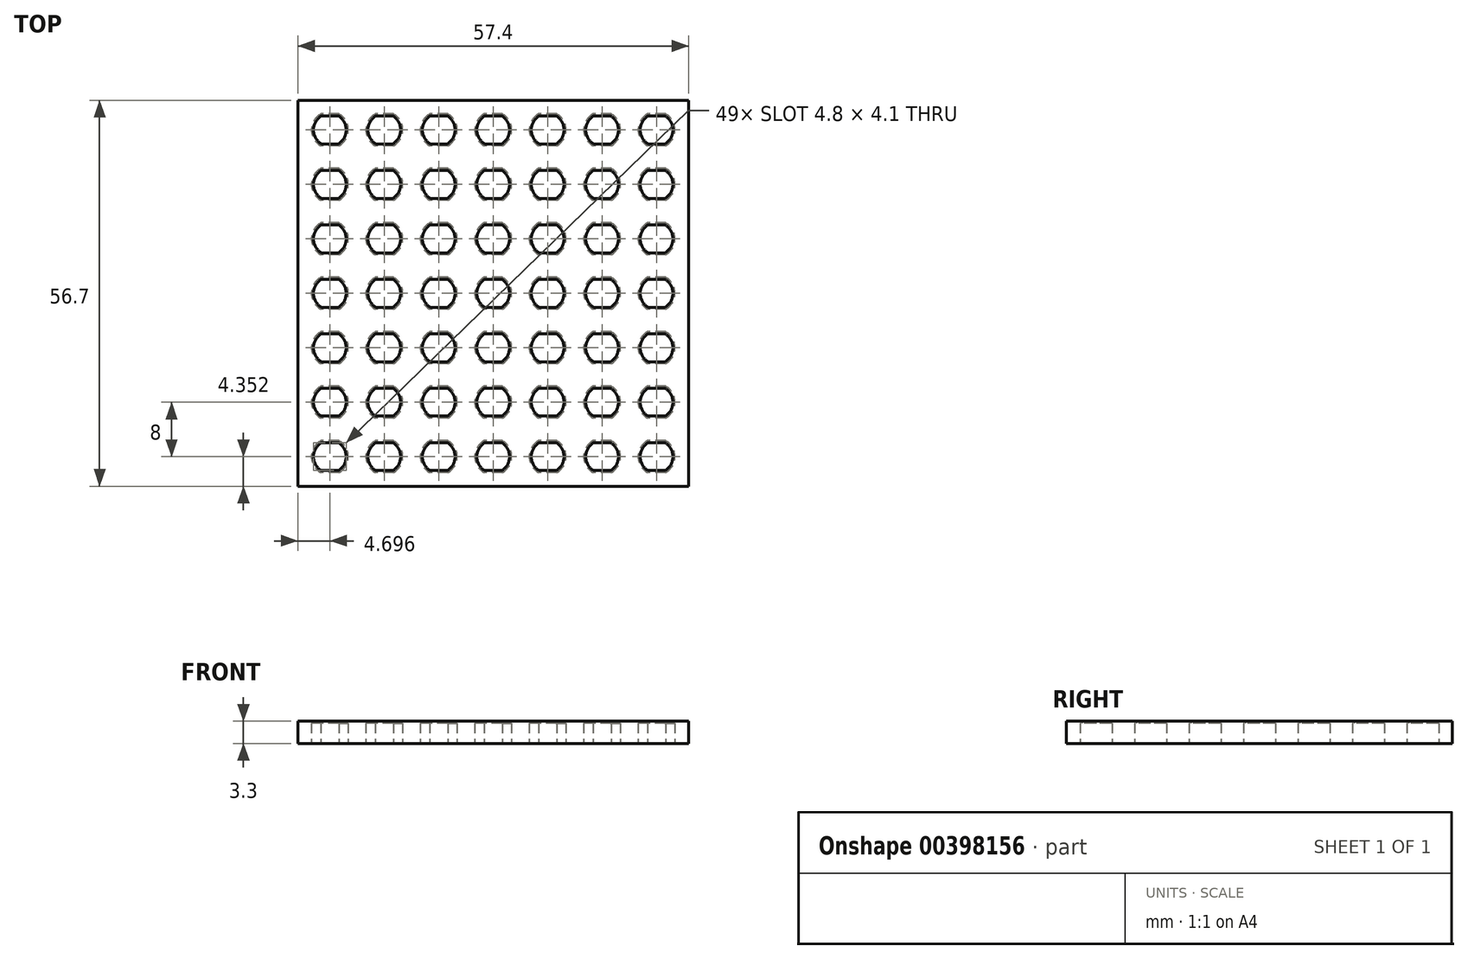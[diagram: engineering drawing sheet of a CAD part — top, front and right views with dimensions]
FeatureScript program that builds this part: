
annotation { "Feature Type Name" : "Feature", "Feature Type Description" : "" }
export const myFeature = defineFeature(function(context is Context, id is Id, definition is map)
    precondition{}
    {
        {
            var Q0;
            Q0=qCreatedBy(makeId("Top.planeOp"),FACE);
            var sketch = newSketch(context, id + "F0", { "sketchPlane" : qUnion([Q0])});
            skLineSegment(sketch, "E0.bottom", {"start": v(27.32, -19.22) * mm, "end": v(-27.32, -19.22) * mm, "construction": true});
            skLineSegment(sketch, "E0.top", {"start": v(27.32, 19.22) * mm, "end": v(-27.32, 19.22) * mm, "construction": true});
            skLineSegment(sketch, "E0.left", {"start": v(27.32, -19.22) * mm, "end": v(27.32, 19.22) * mm, "construction": true});
            skLineSegment(sketch, "E0.right", {"start": v(-27.32, -19.22) * mm, "end": v(-27.32, 19.22) * mm, "construction": true});
            skPoint(sketch, "E0.middle", {"position": v(0, 0) * mm});
            skArc(sketch, "E1", {"start": v(-23.3, 14.17) * mm, "mid": v(-21.92, 16.52) * mm, "end": v(-23.3, 18.87) * mm});
            skLineSegment(sketch, "E2.bottom", {"start": v(-23.3, 18.87) * mm, "end": v(-25.95, 18.87) * mm});
            skLineSegment(sketch, "E2.top", {"start": v(-23.3, 14.17) * mm, "end": v(-25.95, 14.17) * mm});
            skPoint(sketch, "E3.orphan", {"position": v(-21.92, 14.17) * mm});
            skPoint(sketch, "E4.orphan", {"position": v(-21.92, 18.87) * mm});
            skArc(sketch, "E5.trimOffspring", {"start": v(-25.95, 18.87) * mm, "mid": v(-27.32, 16.52) * mm, "end": v(-25.95, 14.17) * mm});
            skArc(sketch, "E6.0.1.0", {"start": v(-25.95, 10.87) * mm, "mid": v(-27.32, 8.52) * mm, "end": v(-25.95, 6.17) * mm});
            skLineSegment(sketch, "E6.0.1.1", {"start": v(-23.3, 6.17) * mm, "end": v(-25.95, 6.17) * mm});
            skLineSegment(sketch, "E6.0.1.2", {"start": v(-23.3, 10.87) * mm, "end": v(-25.95, 10.87) * mm});
            skArc(sketch, "E6.0.1.3", {"start": v(-23.3, 6.17) * mm, "mid": v(-21.92, 8.52) * mm, "end": v(-23.3, 10.87) * mm});
            skArc(sketch, "E6.0.2.0", {"start": v(-25.95, 2.87) * mm, "mid": v(-27.32, 0.52) * mm, "end": v(-25.95, -1.83) * mm});
            skLineSegment(sketch, "E6.0.2.1", {"start": v(-23.3, -1.83) * mm, "end": v(-25.95, -1.83) * mm});
            skLineSegment(sketch, "E6.0.2.2", {"start": v(-23.3, 2.87) * mm, "end": v(-25.95, 2.87) * mm});
            skArc(sketch, "E6.0.2.3", {"start": v(-23.3, -1.83) * mm, "mid": v(-21.92, 0.52) * mm, "end": v(-23.3, 2.87) * mm});
            skArc(sketch, "E6.1.0.0", {"start": v(-17.95, 18.87) * mm, "mid": v(-19.32, 16.52) * mm, "end": v(-17.95, 14.17) * mm});
            skLineSegment(sketch, "E6.1.0.1", {"start": v(-15.3, 14.17) * mm, "end": v(-17.95, 14.17) * mm});
            skLineSegment(sketch, "E6.1.0.2", {"start": v(-15.3, 18.87) * mm, "end": v(-17.95, 18.87) * mm});
            skArc(sketch, "E6.1.0.3", {"start": v(-15.3, 14.17) * mm, "mid": v(-13.92, 16.52) * mm, "end": v(-15.3, 18.87) * mm});
            skArc(sketch, "E6.1.1.0", {"start": v(-17.95, 10.87) * mm, "mid": v(-19.32, 8.52) * mm, "end": v(-17.95, 6.17) * mm});
            skLineSegment(sketch, "E6.1.1.1", {"start": v(-15.3, 6.17) * mm, "end": v(-17.95, 6.17) * mm});
            skLineSegment(sketch, "E6.1.1.2", {"start": v(-15.3, 10.87) * mm, "end": v(-17.95, 10.87) * mm});
            skArc(sketch, "E6.1.1.3", {"start": v(-15.3, 6.17) * mm, "mid": v(-13.92, 8.52) * mm, "end": v(-15.3, 10.87) * mm});
            skArc(sketch, "E6.1.2.0", {"start": v(-17.95, 2.87) * mm, "mid": v(-19.32, 0.52) * mm, "end": v(-17.95, -1.83) * mm});
            skLineSegment(sketch, "E6.1.2.1", {"start": v(-15.3, -1.83) * mm, "end": v(-17.95, -1.83) * mm});
            skLineSegment(sketch, "E6.1.2.2", {"start": v(-15.3, 2.87) * mm, "end": v(-17.95, 2.87) * mm});
            skArc(sketch, "E6.1.2.3", {"start": v(-15.3, -1.83) * mm, "mid": v(-13.92, 0.52) * mm, "end": v(-15.3, 2.87) * mm});
            skArc(sketch, "E6.2.0.0", {"start": v(-9.95, 18.87) * mm, "mid": v(-11.32, 16.52) * mm, "end": v(-9.95, 14.17) * mm});
            skLineSegment(sketch, "E6.2.0.1", {"start": v(-7.3, 14.17) * mm, "end": v(-9.95, 14.17) * mm});
            skLineSegment(sketch, "E6.2.0.2", {"start": v(-7.3, 18.87) * mm, "end": v(-9.95, 18.87) * mm});
            skArc(sketch, "E6.2.0.3", {"start": v(-7.3, 14.17) * mm, "mid": v(-5.92, 16.52) * mm, "end": v(-7.3, 18.87) * mm});
            skArc(sketch, "E6.2.1.0", {"start": v(-9.95, 10.87) * mm, "mid": v(-11.32, 8.52) * mm, "end": v(-9.95, 6.17) * mm});
            skLineSegment(sketch, "E6.2.1.1", {"start": v(-7.3, 6.17) * mm, "end": v(-9.95, 6.17) * mm});
            skLineSegment(sketch, "E6.2.1.2", {"start": v(-7.3, 10.87) * mm, "end": v(-9.95, 10.87) * mm});
            skArc(sketch, "E6.2.1.3", {"start": v(-7.3, 6.17) * mm, "mid": v(-5.92, 8.52) * mm, "end": v(-7.3, 10.87) * mm});
            skArc(sketch, "E6.2.2.0", {"start": v(-9.95, 2.87) * mm, "mid": v(-11.32, 0.52) * mm, "end": v(-9.95, -1.83) * mm});
            skLineSegment(sketch, "E6.2.2.1", {"start": v(-7.3, -1.83) * mm, "end": v(-9.95, -1.83) * mm});
            skLineSegment(sketch, "E6.2.2.2", {"start": v(-7.3, 2.87) * mm, "end": v(-9.95, 2.87) * mm});
            skArc(sketch, "E6.2.2.3", {"start": v(-7.3, -1.83) * mm, "mid": v(-5.92, 0.52) * mm, "end": v(-7.3, 2.87) * mm});
            skArc(sketch, "E6.3.0.0", {"start": v(-1.95, 18.87) * mm, "mid": v(-3.32, 16.52) * mm, "end": v(-1.95, 14.17) * mm});
            skLineSegment(sketch, "E6.3.0.1", {"start": v(0.7, 14.17) * mm, "end": v(-1.95, 14.17) * mm});
            skLineSegment(sketch, "E6.3.0.2", {"start": v(0.7, 18.87) * mm, "end": v(-1.95, 18.87) * mm});
            skArc(sketch, "E6.3.0.3", {"start": v(0.7, 14.17) * mm, "mid": v(2.08, 16.52) * mm, "end": v(0.7, 18.87) * mm});
            skArc(sketch, "E6.3.1.0", {"start": v(-1.95, 10.87) * mm, "mid": v(-3.32, 8.52) * mm, "end": v(-1.95, 6.17) * mm});
            skLineSegment(sketch, "E6.3.1.1", {"start": v(0.7, 6.17) * mm, "end": v(-1.95, 6.17) * mm});
            skLineSegment(sketch, "E6.3.1.2", {"start": v(0.7, 10.87) * mm, "end": v(-1.95, 10.87) * mm});
            skArc(sketch, "E6.3.1.3", {"start": v(0.7, 6.17) * mm, "mid": v(2.08, 8.52) * mm, "end": v(0.7, 10.87) * mm});
            skArc(sketch, "E6.3.2.0", {"start": v(-1.95, 2.87) * mm, "mid": v(-3.32, 0.52) * mm, "end": v(-1.95, -1.83) * mm});
            skLineSegment(sketch, "E6.3.2.1", {"start": v(0.7, -1.83) * mm, "end": v(-1.95, -1.83) * mm});
            skLineSegment(sketch, "E6.3.2.2", {"start": v(0.7, 2.87) * mm, "end": v(-1.95, 2.87) * mm});
            skArc(sketch, "E6.3.2.3", {"start": v(0.7, -1.83) * mm, "mid": v(2.08, 0.52) * mm, "end": v(0.7, 2.87) * mm});
            skLineSegment(sketch, "E6.direction1", {"start": v(-25.95, 14.17) * mm, "end": v(-17.95, 14.17) * mm, "construction": true});
            skLineSegment(sketch, "E6.direction2", {"start": v(-25.95, 14.17) * mm, "end": v(-25.95, 6.17) * mm, "construction": true});
            skLineSegment(sketch, "E7.bottom", {"start": v(-29.32, 20.87) * mm, "end": v(28.08, 20.87) * mm});
            skLineSegment(sketch, "E7.top", {"start": v(-29.32, -35.83) * mm, "end": v(28.08, -35.83) * mm});
            skLineSegment(sketch, "E7.left", {"start": v(-29.32, 20.87) * mm, "end": v(-29.32, -35.83) * mm});
            skLineSegment(sketch, "E7.right", {"start": v(28.08, 20.87) * mm, "end": v(28.08, -35.83) * mm});
            skArc(sketch, "E8.0.4.0", {"start": v(6.05, 18.87) * mm, "mid": v(4.68, 16.52) * mm, "end": v(6.05, 14.17) * mm});
            skLineSegment(sketch, "E8.4.4.0", {"start": v(8.7, 14.17) * mm, "end": v(6.05, 14.17) * mm});
            skLineSegment(sketch, "E8.7.4.0", {"start": v(8.7, 18.87) * mm, "end": v(6.05, 18.87) * mm});
            skArc(sketch, "E8.10.4.0", {"start": v(8.7, 14.17) * mm, "mid": v(10.08, 16.52) * mm, "end": v(8.7, 18.87) * mm});
            skArc(sketch, "E8.0.4.1", {"start": v(6.05, 10.87) * mm, "mid": v(4.68, 8.52) * mm, "end": v(6.05, 6.17) * mm});
            skLineSegment(sketch, "E8.4.4.1", {"start": v(8.7, 6.17) * mm, "end": v(6.05, 6.17) * mm});
            skLineSegment(sketch, "E8.7.4.1", {"start": v(8.7, 10.87) * mm, "end": v(6.05, 10.87) * mm});
            skArc(sketch, "E8.10.4.1", {"start": v(8.7, 6.17) * mm, "mid": v(10.08, 8.52) * mm, "end": v(8.7, 10.87) * mm});
            skArc(sketch, "E8.0.4.2", {"start": v(6.05, 2.87) * mm, "mid": v(4.68, 0.52) * mm, "end": v(6.05, -1.83) * mm});
            skLineSegment(sketch, "E8.4.4.2", {"start": v(8.7, -1.83) * mm, "end": v(6.05, -1.83) * mm});
            skLineSegment(sketch, "E8.7.4.2", {"start": v(8.7, 2.87) * mm, "end": v(6.05, 2.87) * mm});
            skArc(sketch, "E8.10.4.2", {"start": v(8.7, -1.83) * mm, "mid": v(10.08, 0.52) * mm, "end": v(8.7, 2.87) * mm});
            skArc(sketch, "E8.0.5.0", {"start": v(14.05, 18.87) * mm, "mid": v(12.68, 16.52) * mm, "end": v(14.05, 14.17) * mm});
            skLineSegment(sketch, "E8.4.5.0", {"start": v(16.7, 14.17) * mm, "end": v(14.05, 14.17) * mm});
            skLineSegment(sketch, "E8.7.5.0", {"start": v(16.7, 18.87) * mm, "end": v(14.05, 18.87) * mm});
            skArc(sketch, "E8.10.5.0", {"start": v(16.7, 14.17) * mm, "mid": v(18.08, 16.52) * mm, "end": v(16.7, 18.87) * mm});
            skArc(sketch, "E8.0.5.1", {"start": v(14.05, 10.87) * mm, "mid": v(12.68, 8.52) * mm, "end": v(14.05, 6.17) * mm});
            skLineSegment(sketch, "E8.4.5.1", {"start": v(16.7, 6.17) * mm, "end": v(14.05, 6.17) * mm});
            skLineSegment(sketch, "E8.7.5.1", {"start": v(16.7, 10.87) * mm, "end": v(14.05, 10.87) * mm});
            skArc(sketch, "E8.10.5.1", {"start": v(16.7, 6.17) * mm, "mid": v(18.08, 8.52) * mm, "end": v(16.7, 10.87) * mm});
            skArc(sketch, "E8.0.5.2", {"start": v(14.05, 2.87) * mm, "mid": v(12.68, 0.52) * mm, "end": v(14.05, -1.83) * mm});
            skLineSegment(sketch, "E8.4.5.2", {"start": v(16.7, -1.83) * mm, "end": v(14.05, -1.83) * mm});
            skLineSegment(sketch, "E8.7.5.2", {"start": v(16.7, 2.87) * mm, "end": v(14.05, 2.87) * mm});
            skArc(sketch, "E8.10.5.2", {"start": v(16.7, -1.83) * mm, "mid": v(18.08, 0.52) * mm, "end": v(16.7, 2.87) * mm});
            skArc(sketch, "E8.0.6.0", {"start": v(22.05, 18.87) * mm, "mid": v(20.68, 16.52) * mm, "end": v(22.05, 14.17) * mm});
            skLineSegment(sketch, "E8.4.6.0", {"start": v(24.7, 14.17) * mm, "end": v(22.05, 14.17) * mm});
            skLineSegment(sketch, "E8.7.6.0", {"start": v(24.7, 18.87) * mm, "end": v(22.05, 18.87) * mm});
            skArc(sketch, "E8.10.6.0", {"start": v(24.7, 14.17) * mm, "mid": v(26.08, 16.52) * mm, "end": v(24.7, 18.87) * mm});
            skArc(sketch, "E8.0.6.1", {"start": v(22.05, 10.87) * mm, "mid": v(20.68, 8.52) * mm, "end": v(22.05, 6.17) * mm});
            skLineSegment(sketch, "E8.4.6.1", {"start": v(24.7, 6.17) * mm, "end": v(22.05, 6.17) * mm});
            skLineSegment(sketch, "E8.7.6.1", {"start": v(24.7, 10.87) * mm, "end": v(22.05, 10.87) * mm});
            skArc(sketch, "E8.10.6.1", {"start": v(24.7, 6.17) * mm, "mid": v(26.08, 8.52) * mm, "end": v(24.7, 10.87) * mm});
            skArc(sketch, "E8.0.6.2", {"start": v(22.05, 2.87) * mm, "mid": v(20.68, 0.52) * mm, "end": v(22.05, -1.83) * mm});
            skLineSegment(sketch, "E8.4.6.2", {"start": v(24.7, -1.83) * mm, "end": v(22.05, -1.83) * mm});
            skLineSegment(sketch, "E8.7.6.2", {"start": v(24.7, 2.87) * mm, "end": v(22.05, 2.87) * mm});
            skArc(sketch, "E8.10.6.2", {"start": v(24.7, -1.83) * mm, "mid": v(26.08, 0.52) * mm, "end": v(24.7, 2.87) * mm});
            skArc(sketch, "E9.0.0.3", {"start": v(-25.95, -5.13) * mm, "mid": v(-27.32, -7.48) * mm, "end": v(-25.95, -9.83) * mm});
            skLineSegment(sketch, "E9.4.0.3", {"start": v(-23.3, -9.83) * mm, "end": v(-25.95, -9.83) * mm});
            skLineSegment(sketch, "E9.7.0.3", {"start": v(-23.3, -5.13) * mm, "end": v(-25.95, -5.13) * mm});
            skArc(sketch, "E9.10.0.3", {"start": v(-23.3, -9.83) * mm, "mid": v(-21.92, -7.48) * mm, "end": v(-23.3, -5.13) * mm});
            skArc(sketch, "E9.0.0.4", {"start": v(-25.95, -13.13) * mm, "mid": v(-27.32, -15.48) * mm, "end": v(-25.95, -17.83) * mm});
            skLineSegment(sketch, "E9.4.0.4", {"start": v(-23.3, -17.83) * mm, "end": v(-25.95, -17.83) * mm});
            skLineSegment(sketch, "E9.7.0.4", {"start": v(-23.3, -13.13) * mm, "end": v(-25.95, -13.13) * mm});
            skArc(sketch, "E9.10.0.4", {"start": v(-23.3, -17.83) * mm, "mid": v(-21.92, -15.48) * mm, "end": v(-23.3, -13.13) * mm});
            skArc(sketch, "E9.0.0.5", {"start": v(-25.95, -21.13) * mm, "mid": v(-27.32, -23.48) * mm, "end": v(-25.95, -25.83) * mm});
            skLineSegment(sketch, "E9.4.0.5", {"start": v(-23.3, -25.83) * mm, "end": v(-25.95, -25.83) * mm});
            skLineSegment(sketch, "E9.7.0.5", {"start": v(-23.3, -21.13) * mm, "end": v(-25.95, -21.13) * mm});
            skArc(sketch, "E9.10.0.5", {"start": v(-23.3, -25.83) * mm, "mid": v(-21.92, -23.48) * mm, "end": v(-23.3, -21.13) * mm});
            skArc(sketch, "E9.0.0.6", {"start": v(-25.95, -29.13) * mm, "mid": v(-27.32, -31.48) * mm, "end": v(-25.95, -33.83) * mm});
            skLineSegment(sketch, "E9.4.0.6", {"start": v(-23.3, -33.83) * mm, "end": v(-25.95, -33.83) * mm});
            skLineSegment(sketch, "E9.7.0.6", {"start": v(-23.3, -29.13) * mm, "end": v(-25.95, -29.13) * mm});
            skArc(sketch, "E9.10.0.6", {"start": v(-23.3, -33.83) * mm, "mid": v(-21.92, -31.48) * mm, "end": v(-23.3, -29.13) * mm});
            skArc(sketch, "E9.0.1.3", {"start": v(-17.95, -5.13) * mm, "mid": v(-19.32, -7.48) * mm, "end": v(-17.95, -9.83) * mm});
            skLineSegment(sketch, "E9.4.1.3", {"start": v(-15.3, -9.83) * mm, "end": v(-17.95, -9.83) * mm});
            skLineSegment(sketch, "E9.7.1.3", {"start": v(-15.3, -5.13) * mm, "end": v(-17.95, -5.13) * mm});
            skArc(sketch, "E9.10.1.3", {"start": v(-15.3, -9.83) * mm, "mid": v(-13.92, -7.48) * mm, "end": v(-15.3, -5.13) * mm});
            skArc(sketch, "E9.0.1.4", {"start": v(-17.95, -13.13) * mm, "mid": v(-19.32, -15.48) * mm, "end": v(-17.95, -17.83) * mm});
            skLineSegment(sketch, "E9.4.1.4", {"start": v(-15.3, -17.83) * mm, "end": v(-17.95, -17.83) * mm});
            skLineSegment(sketch, "E9.7.1.4", {"start": v(-15.3, -13.13) * mm, "end": v(-17.95, -13.13) * mm});
            skArc(sketch, "E9.10.1.4", {"start": v(-15.3, -17.83) * mm, "mid": v(-13.92, -15.48) * mm, "end": v(-15.3, -13.13) * mm});
            skArc(sketch, "E9.0.1.5", {"start": v(-17.95, -21.13) * mm, "mid": v(-19.32, -23.48) * mm, "end": v(-17.95, -25.83) * mm});
            skLineSegment(sketch, "E9.4.1.5", {"start": v(-15.3, -25.83) * mm, "end": v(-17.95, -25.83) * mm});
            skLineSegment(sketch, "E9.7.1.5", {"start": v(-15.3, -21.13) * mm, "end": v(-17.95, -21.13) * mm});
            skArc(sketch, "E9.10.1.5", {"start": v(-15.3, -25.83) * mm, "mid": v(-13.92, -23.48) * mm, "end": v(-15.3, -21.13) * mm});
            skArc(sketch, "E9.0.1.6", {"start": v(-17.95, -29.13) * mm, "mid": v(-19.32, -31.48) * mm, "end": v(-17.95, -33.83) * mm});
            skLineSegment(sketch, "E9.4.1.6", {"start": v(-15.3, -33.83) * mm, "end": v(-17.95, -33.83) * mm});
            skLineSegment(sketch, "E9.7.1.6", {"start": v(-15.3, -29.13) * mm, "end": v(-17.95, -29.13) * mm});
            skArc(sketch, "E9.10.1.6", {"start": v(-15.3, -33.83) * mm, "mid": v(-13.92, -31.48) * mm, "end": v(-15.3, -29.13) * mm});
            skArc(sketch, "E9.0.2.3", {"start": v(-9.95, -5.13) * mm, "mid": v(-11.32, -7.48) * mm, "end": v(-9.95, -9.83) * mm});
            skLineSegment(sketch, "E9.4.2.3", {"start": v(-7.3, -9.83) * mm, "end": v(-9.95, -9.83) * mm});
            skLineSegment(sketch, "E9.7.2.3", {"start": v(-7.3, -5.13) * mm, "end": v(-9.95, -5.13) * mm});
            skArc(sketch, "E9.10.2.3", {"start": v(-7.3, -9.83) * mm, "mid": v(-5.92, -7.48) * mm, "end": v(-7.3, -5.13) * mm});
            skArc(sketch, "E9.0.2.4", {"start": v(-9.95, -13.13) * mm, "mid": v(-11.32, -15.48) * mm, "end": v(-9.95, -17.83) * mm});
            skLineSegment(sketch, "E9.4.2.4", {"start": v(-7.3, -17.83) * mm, "end": v(-9.95, -17.83) * mm});
            skLineSegment(sketch, "E9.7.2.4", {"start": v(-7.3, -13.13) * mm, "end": v(-9.95, -13.13) * mm});
            skArc(sketch, "E9.10.2.4", {"start": v(-7.3, -17.83) * mm, "mid": v(-5.92, -15.48) * mm, "end": v(-7.3, -13.13) * mm});
            skArc(sketch, "E9.0.2.5", {"start": v(-9.95, -21.13) * mm, "mid": v(-11.32, -23.48) * mm, "end": v(-9.95, -25.83) * mm});
            skLineSegment(sketch, "E9.4.2.5", {"start": v(-7.3, -25.83) * mm, "end": v(-9.95, -25.83) * mm});
            skLineSegment(sketch, "E9.7.2.5", {"start": v(-7.3, -21.13) * mm, "end": v(-9.95, -21.13) * mm});
            skArc(sketch, "E9.10.2.5", {"start": v(-7.3, -25.83) * mm, "mid": v(-5.92, -23.48) * mm, "end": v(-7.3, -21.13) * mm});
            skArc(sketch, "E9.0.2.6", {"start": v(-9.95, -29.13) * mm, "mid": v(-11.32, -31.48) * mm, "end": v(-9.95, -33.83) * mm});
            skLineSegment(sketch, "E9.4.2.6", {"start": v(-7.3, -33.83) * mm, "end": v(-9.95, -33.83) * mm});
            skLineSegment(sketch, "E9.7.2.6", {"start": v(-7.3, -29.13) * mm, "end": v(-9.95, -29.13) * mm});
            skArc(sketch, "E9.10.2.6", {"start": v(-7.3, -33.83) * mm, "mid": v(-5.92, -31.48) * mm, "end": v(-7.3, -29.13) * mm});
            skArc(sketch, "E9.0.3.3", {"start": v(-1.95, -5.13) * mm, "mid": v(-3.32, -7.48) * mm, "end": v(-1.95, -9.83) * mm});
            skLineSegment(sketch, "E9.4.3.3", {"start": v(0.7, -9.83) * mm, "end": v(-1.95, -9.83) * mm});
            skLineSegment(sketch, "E9.7.3.3", {"start": v(0.7, -5.13) * mm, "end": v(-1.95, -5.13) * mm});
            skArc(sketch, "E9.10.3.3", {"start": v(0.7, -9.83) * mm, "mid": v(2.08, -7.48) * mm, "end": v(0.7, -5.13) * mm});
            skArc(sketch, "E9.0.3.4", {"start": v(-1.95, -13.13) * mm, "mid": v(-3.32, -15.48) * mm, "end": v(-1.95, -17.83) * mm});
            skLineSegment(sketch, "E9.4.3.4", {"start": v(0.7, -17.83) * mm, "end": v(-1.95, -17.83) * mm});
            skLineSegment(sketch, "E9.7.3.4", {"start": v(0.7, -13.13) * mm, "end": v(-1.95, -13.13) * mm});
            skArc(sketch, "E9.10.3.4", {"start": v(0.7, -17.83) * mm, "mid": v(2.08, -15.48) * mm, "end": v(0.7, -13.13) * mm});
            skArc(sketch, "E9.0.3.5", {"start": v(-1.95, -21.13) * mm, "mid": v(-3.32, -23.48) * mm, "end": v(-1.95, -25.83) * mm});
            skLineSegment(sketch, "E9.4.3.5", {"start": v(0.7, -25.83) * mm, "end": v(-1.95, -25.83) * mm});
            skLineSegment(sketch, "E9.7.3.5", {"start": v(0.7, -21.13) * mm, "end": v(-1.95, -21.13) * mm});
            skArc(sketch, "E9.10.3.5", {"start": v(0.7, -25.83) * mm, "mid": v(2.08, -23.48) * mm, "end": v(0.7, -21.13) * mm});
            skArc(sketch, "E9.0.3.6", {"start": v(-1.95, -29.13) * mm, "mid": v(-3.32, -31.48) * mm, "end": v(-1.95, -33.83) * mm});
            skLineSegment(sketch, "E9.4.3.6", {"start": v(0.7, -33.83) * mm, "end": v(-1.95, -33.83) * mm});
            skLineSegment(sketch, "E9.7.3.6", {"start": v(0.7, -29.13) * mm, "end": v(-1.95, -29.13) * mm});
            skArc(sketch, "E9.10.3.6", {"start": v(0.7, -33.83) * mm, "mid": v(2.08, -31.48) * mm, "end": v(0.7, -29.13) * mm});
            skArc(sketch, "E9.0.4.3", {"start": v(6.05, -5.13) * mm, "mid": v(4.68, -7.48) * mm, "end": v(6.05, -9.83) * mm});
            skLineSegment(sketch, "E9.4.4.3", {"start": v(8.7, -9.83) * mm, "end": v(6.05, -9.83) * mm});
            skLineSegment(sketch, "E9.7.4.3", {"start": v(8.7, -5.13) * mm, "end": v(6.05, -5.13) * mm});
            skArc(sketch, "E9.10.4.3", {"start": v(8.7, -9.83) * mm, "mid": v(10.08, -7.48) * mm, "end": v(8.7, -5.13) * mm});
            skArc(sketch, "E9.0.4.4", {"start": v(6.05, -13.13) * mm, "mid": v(4.68, -15.48) * mm, "end": v(6.05, -17.83) * mm});
            skLineSegment(sketch, "E9.4.4.4", {"start": v(8.7, -17.83) * mm, "end": v(6.05, -17.83) * mm});
            skLineSegment(sketch, "E9.7.4.4", {"start": v(8.7, -13.13) * mm, "end": v(6.05, -13.13) * mm});
            skArc(sketch, "E9.10.4.4", {"start": v(8.7, -17.83) * mm, "mid": v(10.08, -15.48) * mm, "end": v(8.7, -13.13) * mm});
            skArc(sketch, "E9.0.4.5", {"start": v(6.05, -21.13) * mm, "mid": v(4.68, -23.48) * mm, "end": v(6.05, -25.83) * mm});
            skLineSegment(sketch, "E9.4.4.5", {"start": v(8.7, -25.83) * mm, "end": v(6.05, -25.83) * mm});
            skLineSegment(sketch, "E9.7.4.5", {"start": v(8.7, -21.13) * mm, "end": v(6.05, -21.13) * mm});
            skArc(sketch, "E9.10.4.5", {"start": v(8.7, -25.83) * mm, "mid": v(10.08, -23.48) * mm, "end": v(8.7, -21.13) * mm});
            skArc(sketch, "E9.0.4.6", {"start": v(6.05, -29.13) * mm, "mid": v(4.68, -31.48) * mm, "end": v(6.05, -33.83) * mm});
            skLineSegment(sketch, "E9.4.4.6", {"start": v(8.7, -33.83) * mm, "end": v(6.05, -33.83) * mm});
            skLineSegment(sketch, "E9.7.4.6", {"start": v(8.7, -29.13) * mm, "end": v(6.05, -29.13) * mm});
            skArc(sketch, "E9.10.4.6", {"start": v(8.7, -33.83) * mm, "mid": v(10.08, -31.48) * mm, "end": v(8.7, -29.13) * mm});
            skArc(sketch, "E9.0.5.3", {"start": v(14.05, -5.13) * mm, "mid": v(12.68, -7.48) * mm, "end": v(14.05, -9.83) * mm});
            skLineSegment(sketch, "E9.4.5.3", {"start": v(16.7, -9.83) * mm, "end": v(14.05, -9.83) * mm});
            skLineSegment(sketch, "E9.7.5.3", {"start": v(16.7, -5.13) * mm, "end": v(14.05, -5.13) * mm});
            skArc(sketch, "E9.10.5.3", {"start": v(16.7, -9.83) * mm, "mid": v(18.08, -7.48) * mm, "end": v(16.7, -5.13) * mm});
            skArc(sketch, "E9.0.5.4", {"start": v(14.05, -13.13) * mm, "mid": v(12.68, -15.48) * mm, "end": v(14.05, -17.83) * mm});
            skLineSegment(sketch, "E9.4.5.4", {"start": v(16.7, -17.83) * mm, "end": v(14.05, -17.83) * mm});
            skLineSegment(sketch, "E9.7.5.4", {"start": v(16.7, -13.13) * mm, "end": v(14.05, -13.13) * mm});
            skArc(sketch, "E9.10.5.4", {"start": v(16.7, -17.83) * mm, "mid": v(18.08, -15.48) * mm, "end": v(16.7, -13.13) * mm});
            skArc(sketch, "E9.0.5.5", {"start": v(14.05, -21.13) * mm, "mid": v(12.68, -23.48) * mm, "end": v(14.05, -25.83) * mm});
            skLineSegment(sketch, "E9.4.5.5", {"start": v(16.7, -25.83) * mm, "end": v(14.05, -25.83) * mm});
            skLineSegment(sketch, "E9.7.5.5", {"start": v(16.7, -21.13) * mm, "end": v(14.05, -21.13) * mm});
            skArc(sketch, "E9.10.5.5", {"start": v(16.7, -25.83) * mm, "mid": v(18.08, -23.48) * mm, "end": v(16.7, -21.13) * mm});
            skArc(sketch, "E9.0.5.6", {"start": v(14.05, -29.13) * mm, "mid": v(12.68, -31.48) * mm, "end": v(14.05, -33.83) * mm});
            skLineSegment(sketch, "E9.4.5.6", {"start": v(16.7, -33.83) * mm, "end": v(14.05, -33.83) * mm});
            skLineSegment(sketch, "E9.7.5.6", {"start": v(16.7, -29.13) * mm, "end": v(14.05, -29.13) * mm});
            skArc(sketch, "E9.10.5.6", {"start": v(16.7, -33.83) * mm, "mid": v(18.08, -31.48) * mm, "end": v(16.7, -29.13) * mm});
            skArc(sketch, "E9.0.6.3", {"start": v(22.05, -5.13) * mm, "mid": v(20.68, -7.48) * mm, "end": v(22.05, -9.83) * mm});
            skLineSegment(sketch, "E9.4.6.3", {"start": v(24.7, -9.83) * mm, "end": v(22.05, -9.83) * mm});
            skLineSegment(sketch, "E9.7.6.3", {"start": v(24.7, -5.13) * mm, "end": v(22.05, -5.13) * mm});
            skArc(sketch, "E9.10.6.3", {"start": v(24.7, -9.83) * mm, "mid": v(26.08, -7.48) * mm, "end": v(24.7, -5.13) * mm});
            skArc(sketch, "E9.0.6.4", {"start": v(22.05, -13.13) * mm, "mid": v(20.68, -15.48) * mm, "end": v(22.05, -17.83) * mm});
            skLineSegment(sketch, "E9.4.6.4", {"start": v(24.7, -17.83) * mm, "end": v(22.05, -17.83) * mm});
            skLineSegment(sketch, "E9.7.6.4", {"start": v(24.7, -13.13) * mm, "end": v(22.05, -13.13) * mm});
            skArc(sketch, "E9.10.6.4", {"start": v(24.7, -17.83) * mm, "mid": v(26.08, -15.48) * mm, "end": v(24.7, -13.13) * mm});
            skArc(sketch, "E9.0.6.5", {"start": v(22.05, -21.13) * mm, "mid": v(20.68, -23.48) * mm, "end": v(22.05, -25.83) * mm});
            skLineSegment(sketch, "E9.4.6.5", {"start": v(24.7, -25.83) * mm, "end": v(22.05, -25.83) * mm});
            skLineSegment(sketch, "E9.7.6.5", {"start": v(24.7, -21.13) * mm, "end": v(22.05, -21.13) * mm});
            skArc(sketch, "E9.10.6.5", {"start": v(24.7, -25.83) * mm, "mid": v(26.08, -23.48) * mm, "end": v(24.7, -21.13) * mm});
            skArc(sketch, "E9.0.6.6", {"start": v(22.05, -29.13) * mm, "mid": v(20.68, -31.48) * mm, "end": v(22.05, -33.83) * mm});
            skLineSegment(sketch, "E9.4.6.6", {"start": v(24.7, -33.83) * mm, "end": v(22.05, -33.83) * mm});
            skLineSegment(sketch, "E9.7.6.6", {"start": v(24.7, -29.13) * mm, "end": v(22.05, -29.13) * mm});
            skArc(sketch, "E9.10.6.6", {"start": v(24.7, -33.83) * mm, "mid": v(26.08, -31.48) * mm, "end": v(24.7, -29.13) * mm});
            skSolve(sketch);
        }
        {
            var Q0;
            Q0 = qSketchRegion(id + "F0", true);
            extrude(context, id + "F1", {"entities" : qUnion([Q0]), "depth" : 3 * mm});
        }
        {
            var Q0;
            Q0=makeQuery(id+"F1.opExtrude","CAP_FACE",FACE,{"disambiguationData":[OSD([sQuery(id+"F0.wireOp",EDGE,"E1"),sQuery(id+"F0.wireOp",EDGE,"E2.bottom"),sQuery(id+"F0.wireOp",EDGE,"E2.top"),sQuery(id+"F0.wireOp",EDGE,"E5.trimOffspring"),sQuery(id+"F0.wireOp",EDGE,"E6.0.1.0"),sQuery(id+"F0.wireOp",EDGE,"E6.0.1.1"),sQuery(id+"F0.wireOp",EDGE,"E6.0.1.2"),sQuery(id+"F0.wireOp",EDGE,"E6.0.1.3"),sQuery(id+"F0.wireOp",EDGE,"E6.0.2.0"),sQuery(id+"F0.wireOp",EDGE,"E6.0.2.1"),sQuery(id+"F0.wireOp",EDGE,"E6.0.2.2"),sQuery(id+"F0.wireOp",EDGE,"E6.0.2.3"),sQuery(id+"F0.wireOp",EDGE,"E6.1.0.0"),sQuery(id+"F0.wireOp",EDGE,"E6.1.0.1"),sQuery(id+"F0.wireOp",EDGE,"E6.1.0.2"),sQuery(id+"F0.wireOp",EDGE,"E6.1.0.3"),sQuery(id+"F0.wireOp",EDGE,"E6.1.1.0"),sQuery(id+"F0.wireOp",EDGE,"E6.1.1.1"),sQuery(id+"F0.wireOp",EDGE,"E6.1.1.2"),sQuery(id+"F0.wireOp",EDGE,"E6.1.1.3"),sQuery(id+"F0.wireOp",EDGE,"E6.1.2.0"),sQuery(id+"F0.wireOp",EDGE,"E6.1.2.1"),sQuery(id+"F0.wireOp",EDGE,"E6.1.2.2"),sQuery(id+"F0.wireOp",EDGE,"E6.1.2.3"),sQuery(id+"F0.wireOp",EDGE,"E6.2.0.0"),sQuery(id+"F0.wireOp",EDGE,"E6.2.0.1"),sQuery(id+"F0.wireOp",EDGE,"E6.2.0.2"),sQuery(id+"F0.wireOp",EDGE,"E6.2.0.3"),sQuery(id+"F0.wireOp",EDGE,"E6.2.1.0"),sQuery(id+"F0.wireOp",EDGE,"E6.2.1.1"),sQuery(id+"F0.wireOp",EDGE,"E6.2.1.2"),sQuery(id+"F0.wireOp",EDGE,"E6.2.1.3"),sQuery(id+"F0.wireOp",EDGE,"E6.2.2.0"),sQuery(id+"F0.wireOp",EDGE,"E6.2.2.1"),sQuery(id+"F0.wireOp",EDGE,"E6.2.2.2"),sQuery(id+"F0.wireOp",EDGE,"E6.2.2.3"),sQuery(id+"F0.wireOp",EDGE,"E6.3.0.0"),sQuery(id+"F0.wireOp",EDGE,"E6.3.0.1"),sQuery(id+"F0.wireOp",EDGE,"E6.3.0.2"),sQuery(id+"F0.wireOp",EDGE,"E6.3.0.3"),sQuery(id+"F0.wireOp",EDGE,"E6.3.1.0"),sQuery(id+"F0.wireOp",EDGE,"E6.3.1.1"),sQuery(id+"F0.wireOp",EDGE,"E6.3.1.2"),sQuery(id+"F0.wireOp",EDGE,"E6.3.1.3"),sQuery(id+"F0.wireOp",EDGE,"E6.3.2.0"),sQuery(id+"F0.wireOp",EDGE,"E6.3.2.1"),sQuery(id+"F0.wireOp",EDGE,"E6.3.2.2"),sQuery(id+"F0.wireOp",EDGE,"E6.3.2.3"),sQuery(id+"F0.wireOp",EDGE,"E7.bottom"),sQuery(id+"F0.wireOp",EDGE,"E7.top"),sQuery(id+"F0.wireOp",EDGE,"E7.left"),sQuery(id+"F0.wireOp",EDGE,"E7.right")])],"isStart":false});
            var sketch = newSketch(context, id + "F2", { "sketchPlane" : qUnion([Q0])});
            skLineSegment(sketch, "E10.0", {"start": v(-23.38, 18.57) * mm, "end": v(-25.87, 18.57) * mm});
            skArc(sketch, "E10.1", {"start": v(-23.38, 14.47) * mm, "mid": v(-22.22, 16.52) * mm, "end": v(-23.38, 18.57) * mm});
            skLineSegment(sketch, "E10.2", {"start": v(-23.38, 14.47) * mm, "end": v(-25.87, 14.47) * mm});
            skArc(sketch, "E10.3", {"start": v(-25.87, 18.57) * mm, "mid": v(-27.02, 16.52) * mm, "end": v(-25.87, 14.47) * mm});
            skArc(sketch, "E11.0.1.0", {"start": v(-25.87, 10.57) * mm, "mid": v(-27.02, 8.52) * mm, "end": v(-25.87, 6.47) * mm});
            skLineSegment(sketch, "E11.0.1.1", {"start": v(-23.38, 10.57) * mm, "end": v(-25.87, 10.57) * mm});
            skArc(sketch, "E11.0.1.2", {"start": v(-23.38, 6.47) * mm, "mid": v(-22.22, 8.52) * mm, "end": v(-23.38, 10.57) * mm});
            skLineSegment(sketch, "E11.0.1.3", {"start": v(-23.38, 6.47) * mm, "end": v(-25.87, 6.47) * mm});
            skArc(sketch, "E11.0.2.0", {"start": v(-25.87, 2.57) * mm, "mid": v(-27.02, 0.52) * mm, "end": v(-25.87, -1.53) * mm});
            skLineSegment(sketch, "E11.0.2.1", {"start": v(-23.38, 2.57) * mm, "end": v(-25.87, 2.57) * mm});
            skArc(sketch, "E11.0.2.2", {"start": v(-23.38, -1.53) * mm, "mid": v(-22.22, 0.52) * mm, "end": v(-23.38, 2.57) * mm});
            skLineSegment(sketch, "E11.0.2.3", {"start": v(-23.38, -1.53) * mm, "end": v(-25.87, -1.53) * mm});
            skArc(sketch, "E11.1.0.0", {"start": v(-17.87, 18.57) * mm, "mid": v(-19.02, 16.52) * mm, "end": v(-17.87, 14.47) * mm});
            skLineSegment(sketch, "E11.1.0.1", {"start": v(-15.38, 18.57) * mm, "end": v(-17.87, 18.57) * mm});
            skArc(sketch, "E11.1.0.2", {"start": v(-15.38, 14.47) * mm, "mid": v(-14.22, 16.52) * mm, "end": v(-15.38, 18.57) * mm});
            skLineSegment(sketch, "E11.1.0.3", {"start": v(-15.38, 14.47) * mm, "end": v(-17.87, 14.47) * mm});
            skArc(sketch, "E11.1.1.0", {"start": v(-17.87, 10.57) * mm, "mid": v(-19.02, 8.52) * mm, "end": v(-17.87, 6.47) * mm});
            skLineSegment(sketch, "E11.1.1.1", {"start": v(-15.38, 10.57) * mm, "end": v(-17.87, 10.57) * mm});
            skArc(sketch, "E11.1.1.2", {"start": v(-15.38, 6.47) * mm, "mid": v(-14.22, 8.52) * mm, "end": v(-15.38, 10.57) * mm});
            skLineSegment(sketch, "E11.1.1.3", {"start": v(-15.38, 6.47) * mm, "end": v(-17.87, 6.47) * mm});
            skArc(sketch, "E11.1.2.0", {"start": v(-17.87, 2.57) * mm, "mid": v(-19.02, 0.52) * mm, "end": v(-17.87, -1.53) * mm});
            skLineSegment(sketch, "E11.1.2.1", {"start": v(-15.38, 2.57) * mm, "end": v(-17.87, 2.57) * mm});
            skArc(sketch, "E11.1.2.2", {"start": v(-15.38, -1.53) * mm, "mid": v(-14.22, 0.52) * mm, "end": v(-15.38, 2.57) * mm});
            skLineSegment(sketch, "E11.1.2.3", {"start": v(-15.38, -1.53) * mm, "end": v(-17.87, -1.53) * mm});
            skArc(sketch, "E11.2.0.0", {"start": v(-9.87, 18.57) * mm, "mid": v(-11.02, 16.52) * mm, "end": v(-9.87, 14.47) * mm});
            skLineSegment(sketch, "E11.2.0.1", {"start": v(-7.38, 18.57) * mm, "end": v(-9.87, 18.57) * mm});
            skArc(sketch, "E11.2.0.2", {"start": v(-7.38, 14.47) * mm, "mid": v(-6.22, 16.52) * mm, "end": v(-7.38, 18.57) * mm});
            skLineSegment(sketch, "E11.2.0.3", {"start": v(-7.38, 14.47) * mm, "end": v(-9.87, 14.47) * mm});
            skArc(sketch, "E11.2.1.0", {"start": v(-9.87, 10.57) * mm, "mid": v(-11.02, 8.52) * mm, "end": v(-9.87, 6.47) * mm});
            skLineSegment(sketch, "E11.2.1.1", {"start": v(-7.38, 10.57) * mm, "end": v(-9.87, 10.57) * mm});
            skArc(sketch, "E11.2.1.2", {"start": v(-7.38, 6.47) * mm, "mid": v(-6.22, 8.52) * mm, "end": v(-7.38, 10.57) * mm});
            skLineSegment(sketch, "E11.2.1.3", {"start": v(-7.38, 6.47) * mm, "end": v(-9.87, 6.47) * mm});
            skArc(sketch, "E11.2.2.0", {"start": v(-9.87, 2.57) * mm, "mid": v(-11.02, 0.52) * mm, "end": v(-9.87, -1.53) * mm});
            skLineSegment(sketch, "E11.2.2.1", {"start": v(-7.38, 2.57) * mm, "end": v(-9.87, 2.57) * mm});
            skArc(sketch, "E11.2.2.2", {"start": v(-7.38, -1.53) * mm, "mid": v(-6.22, 0.52) * mm, "end": v(-7.38, 2.57) * mm});
            skLineSegment(sketch, "E11.2.2.3", {"start": v(-7.38, -1.53) * mm, "end": v(-9.87, -1.53) * mm});
            skArc(sketch, "E11.3.0.0", {"start": v(-1.87, 18.57) * mm, "mid": v(-3.02, 16.52) * mm, "end": v(-1.87, 14.47) * mm});
            skLineSegment(sketch, "E11.3.0.1", {"start": v(0.62, 18.57) * mm, "end": v(-1.87, 18.57) * mm});
            skArc(sketch, "E11.3.0.2", {"start": v(0.62, 14.47) * mm, "mid": v(1.78, 16.52) * mm, "end": v(0.62, 18.57) * mm});
            skLineSegment(sketch, "E11.3.0.3", {"start": v(0.62, 14.47) * mm, "end": v(-1.87, 14.47) * mm});
            skArc(sketch, "E11.3.1.0", {"start": v(-1.87, 10.57) * mm, "mid": v(-3.02, 8.52) * mm, "end": v(-1.87, 6.47) * mm});
            skLineSegment(sketch, "E11.3.1.1", {"start": v(0.62, 10.57) * mm, "end": v(-1.87, 10.57) * mm});
            skArc(sketch, "E11.3.1.2", {"start": v(0.62, 6.47) * mm, "mid": v(1.78, 8.52) * mm, "end": v(0.62, 10.57) * mm});
            skLineSegment(sketch, "E11.3.1.3", {"start": v(0.62, 6.47) * mm, "end": v(-1.87, 6.47) * mm});
            skArc(sketch, "E11.3.2.0", {"start": v(-1.87, 2.57) * mm, "mid": v(-3.02, 0.52) * mm, "end": v(-1.87, -1.53) * mm});
            skLineSegment(sketch, "E11.3.2.1", {"start": v(0.62, 2.57) * mm, "end": v(-1.87, 2.57) * mm});
            skArc(sketch, "E11.3.2.2", {"start": v(0.62, -1.53) * mm, "mid": v(1.78, 0.52) * mm, "end": v(0.62, 2.57) * mm});
            skLineSegment(sketch, "E11.3.2.3", {"start": v(0.62, -1.53) * mm, "end": v(-1.87, -1.53) * mm});
            skLineSegment(sketch, "E11.direction1", {"start": v(-25.87, 14.47) * mm, "end": v(-17.87, 14.47) * mm, "construction": true});
            skLineSegment(sketch, "E11.direction2", {"start": v(-25.87, 14.47) * mm, "end": v(-25.87, 6.47) * mm, "construction": true});
            skLineSegment(sketch, "E12.bottom", {"start": v(-29.32, 20.87) * mm, "end": v(28.08, 20.87) * mm});
            skLineSegment(sketch, "E12.top", {"start": v(-29.32, -35.83) * mm, "end": v(28.08, -35.83) * mm});
            skLineSegment(sketch, "E12.left", {"start": v(-29.32, 20.87) * mm, "end": v(-29.32, -35.83) * mm});
            skLineSegment(sketch, "E12.right", {"start": v(28.08, 20.87) * mm, "end": v(28.08, -35.83) * mm});
            skArc(sketch, "E13.0.4.0", {"start": v(6.13, 18.57) * mm, "mid": v(4.98, 16.52) * mm, "end": v(6.13, 14.47) * mm});
            skLineSegment(sketch, "E13.4.4.0", {"start": v(8.62, 18.57) * mm, "end": v(6.13, 18.57) * mm});
            skArc(sketch, "E13.7.4.0", {"start": v(8.62, 14.47) * mm, "mid": v(9.78, 16.52) * mm, "end": v(8.62, 18.57) * mm});
            skLineSegment(sketch, "E13.11.4.0", {"start": v(8.62, 14.47) * mm, "end": v(6.13, 14.47) * mm});
            skArc(sketch, "E13.0.4.1", {"start": v(6.13, 10.57) * mm, "mid": v(4.98, 8.52) * mm, "end": v(6.13, 6.47) * mm});
            skLineSegment(sketch, "E13.4.4.1", {"start": v(8.62, 10.57) * mm, "end": v(6.13, 10.57) * mm});
            skArc(sketch, "E13.7.4.1", {"start": v(8.62, 6.47) * mm, "mid": v(9.78, 8.52) * mm, "end": v(8.62, 10.57) * mm});
            skLineSegment(sketch, "E13.11.4.1", {"start": v(8.62, 6.47) * mm, "end": v(6.13, 6.47) * mm});
            skArc(sketch, "E13.0.4.2", {"start": v(6.13, 2.57) * mm, "mid": v(4.98, 0.52) * mm, "end": v(6.13, -1.53) * mm});
            skLineSegment(sketch, "E13.4.4.2", {"start": v(8.62, 2.57) * mm, "end": v(6.13, 2.57) * mm});
            skArc(sketch, "E13.7.4.2", {"start": v(8.62, -1.53) * mm, "mid": v(9.78, 0.52) * mm, "end": v(8.62, 2.57) * mm});
            skLineSegment(sketch, "E13.11.4.2", {"start": v(8.62, -1.53) * mm, "end": v(6.13, -1.53) * mm});
            skArc(sketch, "E13.0.5.0", {"start": v(14.13, 18.57) * mm, "mid": v(12.98, 16.52) * mm, "end": v(14.13, 14.47) * mm});
            skLineSegment(sketch, "E13.4.5.0", {"start": v(16.62, 18.57) * mm, "end": v(14.13, 18.57) * mm});
            skArc(sketch, "E13.7.5.0", {"start": v(16.62, 14.47) * mm, "mid": v(17.78, 16.52) * mm, "end": v(16.62, 18.57) * mm});
            skLineSegment(sketch, "E13.11.5.0", {"start": v(16.62, 14.47) * mm, "end": v(14.13, 14.47) * mm});
            skArc(sketch, "E13.0.5.1", {"start": v(14.13, 10.57) * mm, "mid": v(12.98, 8.52) * mm, "end": v(14.13, 6.47) * mm});
            skLineSegment(sketch, "E13.4.5.1", {"start": v(16.62, 10.57) * mm, "end": v(14.13, 10.57) * mm});
            skArc(sketch, "E13.7.5.1", {"start": v(16.62, 6.47) * mm, "mid": v(17.78, 8.52) * mm, "end": v(16.62, 10.57) * mm});
            skLineSegment(sketch, "E13.11.5.1", {"start": v(16.62, 6.47) * mm, "end": v(14.13, 6.47) * mm});
            skArc(sketch, "E13.0.5.2", {"start": v(14.13, 2.57) * mm, "mid": v(12.98, 0.52) * mm, "end": v(14.13, -1.53) * mm});
            skLineSegment(sketch, "E13.4.5.2", {"start": v(16.62, 2.57) * mm, "end": v(14.13, 2.57) * mm});
            skArc(sketch, "E13.7.5.2", {"start": v(16.62, -1.53) * mm, "mid": v(17.78, 0.52) * mm, "end": v(16.62, 2.57) * mm});
            skLineSegment(sketch, "E13.11.5.2", {"start": v(16.62, -1.53) * mm, "end": v(14.13, -1.53) * mm});
            skArc(sketch, "E13.0.6.0", {"start": v(22.13, 18.57) * mm, "mid": v(20.98, 16.52) * mm, "end": v(22.13, 14.47) * mm});
            skLineSegment(sketch, "E13.4.6.0", {"start": v(24.62, 18.57) * mm, "end": v(22.13, 18.57) * mm});
            skArc(sketch, "E13.7.6.0", {"start": v(24.62, 14.47) * mm, "mid": v(25.78, 16.52) * mm, "end": v(24.62, 18.57) * mm});
            skLineSegment(sketch, "E13.11.6.0", {"start": v(24.62, 14.47) * mm, "end": v(22.13, 14.47) * mm});
            skArc(sketch, "E13.0.6.1", {"start": v(22.13, 10.57) * mm, "mid": v(20.98, 8.52) * mm, "end": v(22.13, 6.47) * mm});
            skLineSegment(sketch, "E13.4.6.1", {"start": v(24.62, 10.57) * mm, "end": v(22.13, 10.57) * mm});
            skArc(sketch, "E13.7.6.1", {"start": v(24.62, 6.47) * mm, "mid": v(25.78, 8.52) * mm, "end": v(24.62, 10.57) * mm});
            skLineSegment(sketch, "E13.11.6.1", {"start": v(24.62, 6.47) * mm, "end": v(22.13, 6.47) * mm});
            skArc(sketch, "E13.0.6.2", {"start": v(22.13, 2.57) * mm, "mid": v(20.98, 0.52) * mm, "end": v(22.13, -1.53) * mm});
            skLineSegment(sketch, "E13.4.6.2", {"start": v(24.62, 2.57) * mm, "end": v(22.13, 2.57) * mm});
            skArc(sketch, "E13.7.6.2", {"start": v(24.62, -1.53) * mm, "mid": v(25.78, 0.52) * mm, "end": v(24.62, 2.57) * mm});
            skLineSegment(sketch, "E13.11.6.2", {"start": v(24.62, -1.53) * mm, "end": v(22.13, -1.53) * mm});
            skArc(sketch, "E14.0.0.3", {"start": v(-25.87, -5.43) * mm, "mid": v(-27.02, -7.48) * mm, "end": v(-25.87, -9.53) * mm});
            skLineSegment(sketch, "E14.4.0.3", {"start": v(-23.38, -5.43) * mm, "end": v(-25.87, -5.43) * mm});
            skArc(sketch, "E14.7.0.3", {"start": v(-23.38, -9.53) * mm, "mid": v(-22.22, -7.48) * mm, "end": v(-23.38, -5.43) * mm});
            skLineSegment(sketch, "E14.11.0.3", {"start": v(-23.38, -9.53) * mm, "end": v(-25.87, -9.53) * mm});
            skArc(sketch, "E14.0.0.4", {"start": v(-25.87, -13.43) * mm, "mid": v(-27.02, -15.48) * mm, "end": v(-25.87, -17.53) * mm});
            skLineSegment(sketch, "E14.4.0.4", {"start": v(-23.38, -13.43) * mm, "end": v(-25.87, -13.43) * mm});
            skArc(sketch, "E14.7.0.4", {"start": v(-23.38, -17.53) * mm, "mid": v(-22.22, -15.48) * mm, "end": v(-23.38, -13.43) * mm});
            skLineSegment(sketch, "E14.11.0.4", {"start": v(-23.38, -17.53) * mm, "end": v(-25.87, -17.53) * mm});
            skArc(sketch, "E14.0.0.5", {"start": v(-25.87, -21.43) * mm, "mid": v(-27.02, -23.48) * mm, "end": v(-25.87, -25.53) * mm});
            skLineSegment(sketch, "E14.4.0.5", {"start": v(-23.38, -21.43) * mm, "end": v(-25.87, -21.43) * mm});
            skArc(sketch, "E14.7.0.5", {"start": v(-23.38, -25.53) * mm, "mid": v(-22.22, -23.48) * mm, "end": v(-23.38, -21.43) * mm});
            skLineSegment(sketch, "E14.11.0.5", {"start": v(-23.38, -25.53) * mm, "end": v(-25.87, -25.53) * mm});
            skArc(sketch, "E14.0.0.6", {"start": v(-25.87, -29.43) * mm, "mid": v(-27.02, -31.48) * mm, "end": v(-25.87, -33.53) * mm});
            skLineSegment(sketch, "E14.4.0.6", {"start": v(-23.38, -29.43) * mm, "end": v(-25.87, -29.43) * mm});
            skArc(sketch, "E14.7.0.6", {"start": v(-23.38, -33.53) * mm, "mid": v(-22.22, -31.48) * mm, "end": v(-23.38, -29.43) * mm});
            skLineSegment(sketch, "E14.11.0.6", {"start": v(-23.38, -33.53) * mm, "end": v(-25.87, -33.53) * mm});
            skArc(sketch, "E14.0.1.3", {"start": v(-17.87, -5.43) * mm, "mid": v(-19.02, -7.48) * mm, "end": v(-17.87, -9.53) * mm});
            skLineSegment(sketch, "E14.4.1.3", {"start": v(-15.38, -5.43) * mm, "end": v(-17.87, -5.43) * mm});
            skArc(sketch, "E14.7.1.3", {"start": v(-15.38, -9.53) * mm, "mid": v(-14.22, -7.48) * mm, "end": v(-15.38, -5.43) * mm});
            skLineSegment(sketch, "E14.11.1.3", {"start": v(-15.38, -9.53) * mm, "end": v(-17.87, -9.53) * mm});
            skArc(sketch, "E14.0.1.4", {"start": v(-17.87, -13.43) * mm, "mid": v(-19.02, -15.48) * mm, "end": v(-17.87, -17.53) * mm});
            skLineSegment(sketch, "E14.4.1.4", {"start": v(-15.38, -13.43) * mm, "end": v(-17.87, -13.43) * mm});
            skArc(sketch, "E14.7.1.4", {"start": v(-15.38, -17.53) * mm, "mid": v(-14.22, -15.48) * mm, "end": v(-15.38, -13.43) * mm});
            skLineSegment(sketch, "E14.11.1.4", {"start": v(-15.38, -17.53) * mm, "end": v(-17.87, -17.53) * mm});
            skArc(sketch, "E14.0.1.5", {"start": v(-17.87, -21.43) * mm, "mid": v(-19.02, -23.48) * mm, "end": v(-17.87, -25.53) * mm});
            skLineSegment(sketch, "E14.4.1.5", {"start": v(-15.38, -21.43) * mm, "end": v(-17.87, -21.43) * mm});
            skArc(sketch, "E14.7.1.5", {"start": v(-15.38, -25.53) * mm, "mid": v(-14.22, -23.48) * mm, "end": v(-15.38, -21.43) * mm});
            skLineSegment(sketch, "E14.11.1.5", {"start": v(-15.38, -25.53) * mm, "end": v(-17.87, -25.53) * mm});
            skArc(sketch, "E14.0.1.6", {"start": v(-17.87, -29.43) * mm, "mid": v(-19.02, -31.48) * mm, "end": v(-17.87, -33.53) * mm});
            skLineSegment(sketch, "E14.4.1.6", {"start": v(-15.38, -29.43) * mm, "end": v(-17.87, -29.43) * mm});
            skArc(sketch, "E14.7.1.6", {"start": v(-15.38, -33.53) * mm, "mid": v(-14.22, -31.48) * mm, "end": v(-15.38, -29.43) * mm});
            skLineSegment(sketch, "E14.11.1.6", {"start": v(-15.38, -33.53) * mm, "end": v(-17.87, -33.53) * mm});
            skArc(sketch, "E14.0.2.3", {"start": v(-9.87, -5.43) * mm, "mid": v(-11.02, -7.48) * mm, "end": v(-9.87, -9.53) * mm});
            skLineSegment(sketch, "E14.4.2.3", {"start": v(-7.38, -5.43) * mm, "end": v(-9.87, -5.43) * mm});
            skArc(sketch, "E14.7.2.3", {"start": v(-7.38, -9.53) * mm, "mid": v(-6.22, -7.48) * mm, "end": v(-7.38, -5.43) * mm});
            skLineSegment(sketch, "E14.11.2.3", {"start": v(-7.38, -9.53) * mm, "end": v(-9.87, -9.53) * mm});
            skArc(sketch, "E14.0.2.4", {"start": v(-9.87, -13.43) * mm, "mid": v(-11.02, -15.48) * mm, "end": v(-9.87, -17.53) * mm});
            skLineSegment(sketch, "E14.4.2.4", {"start": v(-7.38, -13.43) * mm, "end": v(-9.87, -13.43) * mm});
            skArc(sketch, "E14.7.2.4", {"start": v(-7.38, -17.53) * mm, "mid": v(-6.22, -15.48) * mm, "end": v(-7.38, -13.43) * mm});
            skLineSegment(sketch, "E14.11.2.4", {"start": v(-7.38, -17.53) * mm, "end": v(-9.87, -17.53) * mm});
            skArc(sketch, "E14.0.2.5", {"start": v(-9.87, -21.43) * mm, "mid": v(-11.02, -23.48) * mm, "end": v(-9.87, -25.53) * mm});
            skLineSegment(sketch, "E14.4.2.5", {"start": v(-7.38, -21.43) * mm, "end": v(-9.87, -21.43) * mm});
            skArc(sketch, "E14.7.2.5", {"start": v(-7.38, -25.53) * mm, "mid": v(-6.22, -23.48) * mm, "end": v(-7.38, -21.43) * mm});
            skLineSegment(sketch, "E14.11.2.5", {"start": v(-7.38, -25.53) * mm, "end": v(-9.87, -25.53) * mm});
            skArc(sketch, "E14.0.2.6", {"start": v(-9.87, -29.43) * mm, "mid": v(-11.02, -31.48) * mm, "end": v(-9.87, -33.53) * mm});
            skLineSegment(sketch, "E14.4.2.6", {"start": v(-7.38, -29.43) * mm, "end": v(-9.87, -29.43) * mm});
            skArc(sketch, "E14.7.2.6", {"start": v(-7.38, -33.53) * mm, "mid": v(-6.22, -31.48) * mm, "end": v(-7.38, -29.43) * mm});
            skLineSegment(sketch, "E14.11.2.6", {"start": v(-7.38, -33.53) * mm, "end": v(-9.87, -33.53) * mm});
            skArc(sketch, "E14.0.3.3", {"start": v(-1.87, -5.43) * mm, "mid": v(-3.02, -7.48) * mm, "end": v(-1.87, -9.53) * mm});
            skLineSegment(sketch, "E14.4.3.3", {"start": v(0.62, -5.43) * mm, "end": v(-1.87, -5.43) * mm});
            skArc(sketch, "E14.7.3.3", {"start": v(0.62, -9.53) * mm, "mid": v(1.78, -7.48) * mm, "end": v(0.62, -5.43) * mm});
            skLineSegment(sketch, "E14.11.3.3", {"start": v(0.62, -9.53) * mm, "end": v(-1.87, -9.53) * mm});
            skArc(sketch, "E14.0.3.4", {"start": v(-1.87, -13.43) * mm, "mid": v(-3.02, -15.48) * mm, "end": v(-1.87, -17.53) * mm});
            skLineSegment(sketch, "E14.4.3.4", {"start": v(0.62, -13.43) * mm, "end": v(-1.87, -13.43) * mm});
            skArc(sketch, "E14.7.3.4", {"start": v(0.62, -17.53) * mm, "mid": v(1.78, -15.48) * mm, "end": v(0.62, -13.43) * mm});
            skLineSegment(sketch, "E14.11.3.4", {"start": v(0.62, -17.53) * mm, "end": v(-1.87, -17.53) * mm});
            skArc(sketch, "E14.0.3.5", {"start": v(-1.87, -21.43) * mm, "mid": v(-3.02, -23.48) * mm, "end": v(-1.87, -25.53) * mm});
            skLineSegment(sketch, "E14.4.3.5", {"start": v(0.62, -21.43) * mm, "end": v(-1.87, -21.43) * mm});
            skArc(sketch, "E14.7.3.5", {"start": v(0.62, -25.53) * mm, "mid": v(1.78, -23.48) * mm, "end": v(0.62, -21.43) * mm});
            skLineSegment(sketch, "E14.11.3.5", {"start": v(0.62, -25.53) * mm, "end": v(-1.87, -25.53) * mm});
            skArc(sketch, "E14.0.3.6", {"start": v(-1.87, -29.43) * mm, "mid": v(-3.02, -31.48) * mm, "end": v(-1.87, -33.53) * mm});
            skLineSegment(sketch, "E14.4.3.6", {"start": v(0.62, -29.43) * mm, "end": v(-1.87, -29.43) * mm});
            skArc(sketch, "E14.7.3.6", {"start": v(0.62, -33.53) * mm, "mid": v(1.78, -31.48) * mm, "end": v(0.62, -29.43) * mm});
            skLineSegment(sketch, "E14.11.3.6", {"start": v(0.62, -33.53) * mm, "end": v(-1.87, -33.53) * mm});
            skArc(sketch, "E14.0.4.3", {"start": v(6.13, -5.43) * mm, "mid": v(4.98, -7.48) * mm, "end": v(6.13, -9.53) * mm});
            skLineSegment(sketch, "E14.4.4.3", {"start": v(8.62, -5.43) * mm, "end": v(6.13, -5.43) * mm});
            skArc(sketch, "E14.7.4.3", {"start": v(8.62, -9.53) * mm, "mid": v(9.78, -7.48) * mm, "end": v(8.62, -5.43) * mm});
            skLineSegment(sketch, "E14.11.4.3", {"start": v(8.62, -9.53) * mm, "end": v(6.13, -9.53) * mm});
            skArc(sketch, "E14.0.4.4", {"start": v(6.13, -13.43) * mm, "mid": v(4.98, -15.48) * mm, "end": v(6.13, -17.53) * mm});
            skLineSegment(sketch, "E14.4.4.4", {"start": v(8.62, -13.43) * mm, "end": v(6.13, -13.43) * mm});
            skArc(sketch, "E14.7.4.4", {"start": v(8.62, -17.53) * mm, "mid": v(9.78, -15.48) * mm, "end": v(8.62, -13.43) * mm});
            skLineSegment(sketch, "E14.11.4.4", {"start": v(8.62, -17.53) * mm, "end": v(6.13, -17.53) * mm});
            skArc(sketch, "E14.0.4.5", {"start": v(6.13, -21.43) * mm, "mid": v(4.98, -23.48) * mm, "end": v(6.13, -25.53) * mm});
            skLineSegment(sketch, "E14.4.4.5", {"start": v(8.62, -21.43) * mm, "end": v(6.13, -21.43) * mm});
            skArc(sketch, "E14.7.4.5", {"start": v(8.62, -25.53) * mm, "mid": v(9.78, -23.48) * mm, "end": v(8.62, -21.43) * mm});
            skLineSegment(sketch, "E14.11.4.5", {"start": v(8.62, -25.53) * mm, "end": v(6.13, -25.53) * mm});
            skArc(sketch, "E14.0.4.6", {"start": v(6.13, -29.43) * mm, "mid": v(4.98, -31.48) * mm, "end": v(6.13, -33.53) * mm});
            skLineSegment(sketch, "E14.4.4.6", {"start": v(8.62, -29.43) * mm, "end": v(6.13, -29.43) * mm});
            skArc(sketch, "E14.7.4.6", {"start": v(8.62, -33.53) * mm, "mid": v(9.78, -31.48) * mm, "end": v(8.62, -29.43) * mm});
            skLineSegment(sketch, "E14.11.4.6", {"start": v(8.62, -33.53) * mm, "end": v(6.13, -33.53) * mm});
            skArc(sketch, "E14.0.5.3", {"start": v(14.13, -5.43) * mm, "mid": v(12.98, -7.48) * mm, "end": v(14.13, -9.53) * mm});
            skLineSegment(sketch, "E14.4.5.3", {"start": v(16.62, -5.43) * mm, "end": v(14.13, -5.43) * mm});
            skArc(sketch, "E14.7.5.3", {"start": v(16.62, -9.53) * mm, "mid": v(17.78, -7.48) * mm, "end": v(16.62, -5.43) * mm});
            skLineSegment(sketch, "E14.11.5.3", {"start": v(16.62, -9.53) * mm, "end": v(14.13, -9.53) * mm});
            skArc(sketch, "E14.0.5.4", {"start": v(14.13, -13.43) * mm, "mid": v(12.98, -15.48) * mm, "end": v(14.13, -17.53) * mm});
            skLineSegment(sketch, "E14.4.5.4", {"start": v(16.62, -13.43) * mm, "end": v(14.13, -13.43) * mm});
            skArc(sketch, "E14.7.5.4", {"start": v(16.62, -17.53) * mm, "mid": v(17.78, -15.48) * mm, "end": v(16.62, -13.43) * mm});
            skLineSegment(sketch, "E14.11.5.4", {"start": v(16.62, -17.53) * mm, "end": v(14.13, -17.53) * mm});
            skArc(sketch, "E14.0.5.5", {"start": v(14.13, -21.43) * mm, "mid": v(12.98, -23.48) * mm, "end": v(14.13, -25.53) * mm});
            skLineSegment(sketch, "E14.4.5.5", {"start": v(16.62, -21.43) * mm, "end": v(14.13, -21.43) * mm});
            skArc(sketch, "E14.7.5.5", {"start": v(16.62, -25.53) * mm, "mid": v(17.78, -23.48) * mm, "end": v(16.62, -21.43) * mm});
            skLineSegment(sketch, "E14.11.5.5", {"start": v(16.62, -25.53) * mm, "end": v(14.13, -25.53) * mm});
            skArc(sketch, "E14.0.5.6", {"start": v(14.13, -29.43) * mm, "mid": v(12.98, -31.48) * mm, "end": v(14.13, -33.53) * mm});
            skLineSegment(sketch, "E14.4.5.6", {"start": v(16.62, -29.43) * mm, "end": v(14.13, -29.43) * mm});
            skArc(sketch, "E14.7.5.6", {"start": v(16.62, -33.53) * mm, "mid": v(17.78, -31.48) * mm, "end": v(16.62, -29.43) * mm});
            skLineSegment(sketch, "E14.11.5.6", {"start": v(16.62, -33.53) * mm, "end": v(14.13, -33.53) * mm});
            skArc(sketch, "E14.0.6.3", {"start": v(22.13, -5.43) * mm, "mid": v(20.98, -7.48) * mm, "end": v(22.13, -9.53) * mm});
            skLineSegment(sketch, "E14.4.6.3", {"start": v(24.62, -5.43) * mm, "end": v(22.13, -5.43) * mm});
            skArc(sketch, "E14.7.6.3", {"start": v(24.62, -9.53) * mm, "mid": v(25.78, -7.48) * mm, "end": v(24.62, -5.43) * mm});
            skLineSegment(sketch, "E14.11.6.3", {"start": v(24.62, -9.53) * mm, "end": v(22.13, -9.53) * mm});
            skArc(sketch, "E14.0.6.4", {"start": v(22.13, -13.43) * mm, "mid": v(20.98, -15.48) * mm, "end": v(22.13, -17.53) * mm});
            skLineSegment(sketch, "E14.4.6.4", {"start": v(24.62, -13.43) * mm, "end": v(22.13, -13.43) * mm});
            skArc(sketch, "E14.7.6.4", {"start": v(24.62, -17.53) * mm, "mid": v(25.78, -15.48) * mm, "end": v(24.62, -13.43) * mm});
            skLineSegment(sketch, "E14.11.6.4", {"start": v(24.62, -17.53) * mm, "end": v(22.13, -17.53) * mm});
            skArc(sketch, "E14.0.6.5", {"start": v(22.13, -21.43) * mm, "mid": v(20.98, -23.48) * mm, "end": v(22.13, -25.53) * mm});
            skLineSegment(sketch, "E14.4.6.5", {"start": v(24.62, -21.43) * mm, "end": v(22.13, -21.43) * mm});
            skArc(sketch, "E14.7.6.5", {"start": v(24.62, -25.53) * mm, "mid": v(25.78, -23.48) * mm, "end": v(24.62, -21.43) * mm});
            skLineSegment(sketch, "E14.11.6.5", {"start": v(24.62, -25.53) * mm, "end": v(22.13, -25.53) * mm});
            skArc(sketch, "E14.0.6.6", {"start": v(22.13, -29.43) * mm, "mid": v(20.98, -31.48) * mm, "end": v(22.13, -33.53) * mm});
            skLineSegment(sketch, "E14.4.6.6", {"start": v(24.62, -29.43) * mm, "end": v(22.13, -29.43) * mm});
            skArc(sketch, "E14.7.6.6", {"start": v(24.62, -33.53) * mm, "mid": v(25.78, -31.48) * mm, "end": v(24.62, -29.43) * mm});
            skLineSegment(sketch, "E14.11.6.6", {"start": v(24.62, -33.53) * mm, "end": v(22.13, -33.53) * mm});
            skSolve(sketch);
        }
        {
            var Q0;
            Q0 = qSketchRegion(id + "F2", true);
            extrude(context, id + "F3", {"entities" : qUnion([Q0]), "operationType" : NewBodyOperationType.ADD, "depth" : 0.3 * mm});
        }
    });
